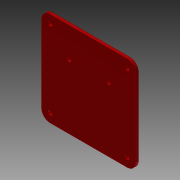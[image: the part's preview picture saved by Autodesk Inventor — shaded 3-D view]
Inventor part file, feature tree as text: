
AUTODESK INVENTOR PART (.ipt)
format: ipt  version: 2015 (Build 190159000, 159)  size: 104,960 bytes
history: native  units: in
note: dims shown in document units (in); Inventor stores cm internally (conversion verified against a paired STEP export)
features: sketch x3, extrude x2, hole x1
ambient origin geometry x8: Origin, YZ Plane, XZ Plane, XY Plane, X Axis, Y Axis, Z Axis, Center Point
bodies: Solid1 (feature_tree)
feature tree (6):
  extrude  "Extrusion1"  Depth=2.75in
  hole  "Hole1"  [1 undecoded]
  extrude  "Extrusion2"  Depth=0.25in
  sketch  "Sketch1"  dims[d0=2.75in d1=2.75in]
  sketch  "Sketch2"  dims[d2=0.25in d3=0.08in d4=0.0in]
  sketch  "Sketch3"  dims[d5=0.126in d6=0.75in d7=0.2205in d8=0.25in d9=90.0deg d10=1.0in d11=0.8108in d12=0.126in d13=1.15in d14=0.5in d15=0.575in d16=0.15in d17=0.0in d22=0.126in]
note: 1 required parameter value undecoded (feature->parameter linkage not recoverable at this tier; creation-order binding heuristic only, values carry confidence <= 0.55)
